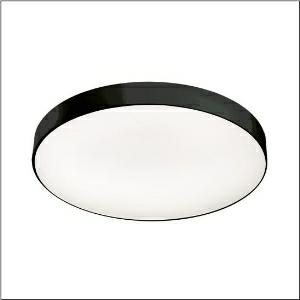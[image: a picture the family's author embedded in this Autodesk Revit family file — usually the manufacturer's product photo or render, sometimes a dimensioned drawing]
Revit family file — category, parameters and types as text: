
# Revit family: round_21_l_51mr38nd0321b
name_source: partatom
category: Lighting Fixtures
units: mm (PartAtom-declared; Revit-internal decimal feet)

## family parameters
Cut with Voids When Loaded = No
Host = Face
Light Source = No
Part Type = Normal
Room Calculation Point = No
Round Connector Dimension = Use Diameter
Shared = No

## types (1)
- Round 21 L (1 x LED, 11740 lm, 88.2 W, 3000K)
    Apparent Load = 88 VA
    CIE Flux Codes = 66 90 98 71 100
    Color Rendering = 80
    Color Temperature = 3000K
    Default Elevation = 1800 mm
    Description = Round 21 L, wall and ceiling luminaire, primary optical cover: micro prismatic cover, of PMMA, transparent, CAT 2 (L<= 3000cd/m²), light emission: direct/indirect distribution, primary light characteristic: symmetric, installation type: suspended mounting, surface-mounted, LED, rated luminous flux: 11.740lm, luminous efficacy: 133lm/W, light colour: 830, colour temperature: 3000K, control gear: DALI 2, with terminal, 5-pole, mains connection: 230V, AC, 50/60Hz, rated input power: 88.2W, housing, of aluminium, coated, black, diameter: 850mm, height: 62mm, protection rating (complete): IP40, insulation class (complete): insulation class I (protective earthing), certification: CE, impact resistance: IK04, permissible operating ambient temperature: -10..+35°C, packaging unit: 1 piece
    Height = 87 mm
    Lamp = 1 x LED
    Lamp Light Flux = 11740 lm
    Lamp Power = 88.2 W
    Lamp count = 1
    Length = 850 mm
    Luminous efficacy = 133 lm/W
    Manufacturer = Siteco
    ModVariant = No
    Model = 51MR38ND0321B
    Mounting Place = Ceiling
    Mounting Type = Surface mounted
    Number of Poles = 1
    OnlyDefault = Yes
    Power Factor = 1
    Product Name = Round 21 L
    Product group = wall and ceiling luminaire | ceiling mounted
    ProductGroupID = 305
    Protection Class = Protection class I
    Protection Degree = IP 40
    RLX_Detail_Level = 1
    RLX_Emergency_Light_Flux = 0 lm
    RLX_Emergency_Type = 0
    RLX_Emergency_Type_DB = No
    RlxData = <blob elided: 28741 chars, md5=8d0798aa>
    Socket = socket
    Standby Power = 0 W
    System Light Flux = 11740 lm
    System Power = 88 W
    Type Comments = Product without accessories
    Type Image = l_1258326.jpg
    URL = http://relux.com
    VarID = ---
    Voltage = 0 V
    Weight = 0.00 kg
    Width = 0 mm  [stored 0 ft]

note: [stored X ft] marks values corroborated as IEEE doubles in the binary element streams (Revit-internal decimal feet)

## geometry (parser evidence)
native form markers: Blend x4, Sweep x12
no freeform markers — native parametric forms only
